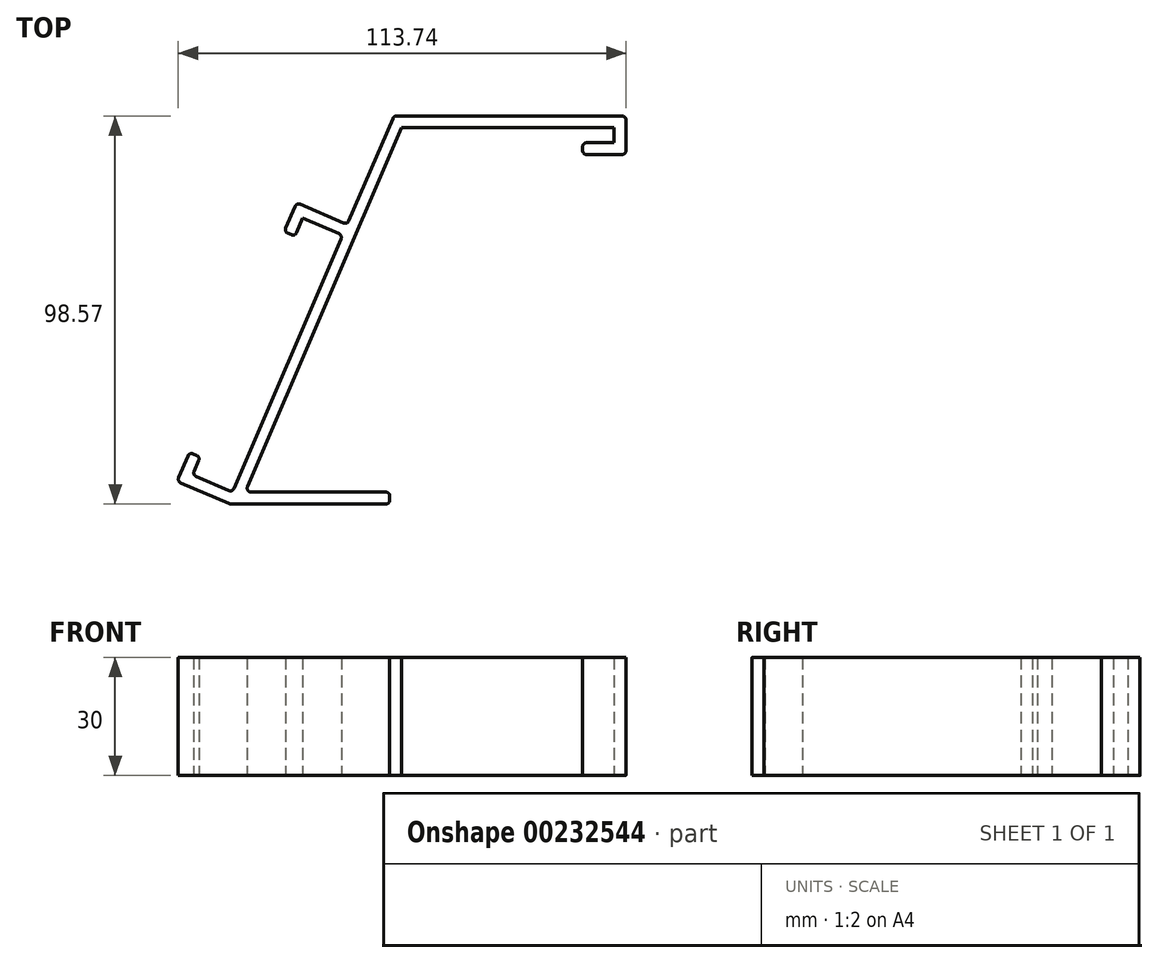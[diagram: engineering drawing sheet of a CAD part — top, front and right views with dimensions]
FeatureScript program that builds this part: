
annotation { "Feature Type Name" : "Feature", "Feature Type Description" : "" }
export const myFeature = defineFeature(function(context is Context, id is Id, definition is map)
    precondition{}
    {
        {
            var Q0;
            Q0=qCreatedBy(makeId("Top.planeOp"),FACE);
            var sketch = newSketch(context, id + "F0", { "sketchPlane" : qUnion([Q0])});
            skLineSegment(sketch, "E0", {"start": v(12.49, -12.5) * mm, "end": v(19.49, -12.5) * mm});
            skLineSegment(sketch, "E1", {"start": v(19.49, -12.5) * mm, "end": v(19.49, -8.7) * mm});
            skLineSegment(sketch, "E2", {"start": v(19.49, -8.7) * mm, "end": v(-34.51, -8.7) * mm});
            skLineSegment(sketch, "E3", {"start": v(21.5, -15.5) * mm, "end": v(12.49, -15.5) * mm});
            skLineSegment(sketch, "E4", {"start": v(11.49, -13.49) * mm, "end": v(11.49, -14.5) * mm});
            skLineSegment(sketch, "E5", {"start": v(-34.51, -8.7) * mm, "end": v(-73.65, -99.87) * mm});
            skLineSegment(sketch, "E6", {"start": v(-72.73, -101.26) * mm, "end": v(-38.5, -101.26) * mm});
            skLineSegment(sketch, "E7", {"start": v(-37.51, -102.26) * mm, "end": v(-37.51, -103.26) * mm});
            skLineSegment(sketch, "E8", {"start": v(-38.5, -104.26) * mm, "end": v(-77.92, -104.26) * mm});
            skLineSegment(sketch, "E9", {"start": v(-86.7, -97.31) * mm, "end": v(-78.43, -100.86) * mm});
            skLineSegment(sketch, "E10", {"start": v(-77.12, -100.34) * mm, "end": v(-49.9, -36.93) * mm});
            skLineSegment(sketch, "E11", {"start": v(-87.23, -96) * mm, "end": v(-86.04, -93.24) * mm});
            skLineSegment(sketch, "E12", {"start": v(-86.56, -91.93) * mm, "end": v(-87.49, -91.53) * mm});
            skLineSegment(sketch, "E13", {"start": v(-88.8, -92.06) * mm, "end": v(-91.17, -97.58) * mm});
            skLineSegment(sketch, "E14", {"start": v(-90.64, -98.89) * mm, "end": v(-78.32, -104.18) * mm});
            skLineSegment(sketch, "E15", {"start": v(-50.42, -35.62) * mm, "end": v(-59.61, -31.68) * mm});
            skLineSegment(sketch, "E16", {"start": v(-59.61, -31.68) * mm, "end": v(-61.2, -35.35) * mm});
            skLineSegment(sketch, "E17", {"start": v(-62.5, -35.88) * mm, "end": v(-63.43, -35.48) * mm});
            skLineSegment(sketch, "E18", {"start": v(-63.95, -34.17) * mm, "end": v(-61.58, -28.65) * mm});
            skLineSegment(sketch, "E19", {"start": v(-60.27, -28.13) * mm, "end": v(-49.24, -32.86) * mm});
            skLineSegment(sketch, "E20.trimOffspring", {"start": v(-47.93, -32.34) * mm, "end": v(-36.75, -6.3) * mm});
            skLineSegment(sketch, "E21", {"start": v(22.49, -14.5) * mm, "end": v(22.49, -6.69) * mm});
            skLineSegment(sketch, "E22", {"start": v(-35.83, -5.7) * mm, "end": v(21.5, -5.7) * mm});
            skPoint(sketch, "E23.visualSharp", {"position": v(11.49, -12.5) * mm});
            skArc(sketch, "E23.filletArc", {"start": v(12.49, -12.5) * mm, "mid": v(11.78, -12.78) * mm, "end": v(11.49, -13.49) * mm});
            skPoint(sketch, "E24.visualSharp", {"position": v(11.49, -15.5) * mm});
            skArc(sketch, "E24.filletArc", {"start": v(11.49, -14.5) * mm, "mid": v(11.78, -15.2) * mm, "end": v(12.49, -15.5) * mm});
            skPoint(sketch, "E25.visualSharp", {"position": v(22.49, -15.5) * mm});
            skArc(sketch, "E25.filletArc", {"start": v(21.5, -15.5) * mm, "mid": v(22.2, -15.2) * mm, "end": v(22.49, -14.5) * mm});
            skPoint(sketch, "E26.visualSharp", {"position": v(22.49, -5.7) * mm});
            skArc(sketch, "E26.filletArc", {"start": v(22.49, -6.69) * mm, "mid": v(22.2, -5.98) * mm, "end": v(21.5, -5.7) * mm});
            skPoint(sketch, "E27.visualSharp", {"position": v(-36.49, -5.7) * mm});
            skArc(sketch, "E27.filletArc", {"start": v(-35.83, -5.7) * mm, "mid": v(-36.38, -5.86) * mm, "end": v(-36.75, -6.3) * mm});
            skPoint(sketch, "E28.visualSharp", {"position": v(-61.19, -27.74) * mm});
            skArc(sketch, "E28.filletArc", {"start": v(-60.27, -28.13) * mm, "mid": v(-61.03, -28.12) * mm, "end": v(-61.58, -28.65) * mm});
            skPoint(sketch, "E29.visualSharp", {"position": v(-64.34, -35.09) * mm});
            skArc(sketch, "E29.filletArc", {"start": v(-63.95, -34.17) * mm, "mid": v(-63.96, -34.93) * mm, "end": v(-63.43, -35.48) * mm});
            skPoint(sketch, "E30.visualSharp", {"position": v(-61.58, -36.27) * mm});
            skArc(sketch, "E30.filletArc", {"start": v(-62.5, -35.88) * mm, "mid": v(-61.74, -35.89) * mm, "end": v(-61.2, -35.35) * mm});
            skPoint(sketch, "E31.visualSharp", {"position": v(-48.32, -33.26) * mm});
            skArc(sketch, "E31.filletArc", {"start": v(-49.24, -32.86) * mm, "mid": v(-48.47, -32.87) * mm, "end": v(-47.93, -32.34) * mm});
            skPoint(sketch, "E32.visualSharp", {"position": v(-49.5, -36.01) * mm});
            skArc(sketch, "E32.filletArc", {"start": v(-49.9, -36.93) * mm, "mid": v(-49.89, -36.17) * mm, "end": v(-50.42, -35.62) * mm});
            skPoint(sketch, "E33.visualSharp", {"position": v(-77.51, -101.26) * mm});
            skArc(sketch, "E33.filletArc", {"start": v(-78.43, -100.86) * mm, "mid": v(-77.66, -100.87) * mm, "end": v(-77.12, -100.34) * mm});
            skPoint(sketch, "E34.visualSharp", {"position": v(-78.13, -104.26) * mm});
            skArc(sketch, "E34.filletArc", {"start": v(-78.32, -104.18) * mm, "mid": v(-78.12, -104.24) * mm, "end": v(-77.92, -104.26) * mm});
            skPoint(sketch, "E35.visualSharp", {"position": v(-74.25, -101.26) * mm});
            skArc(sketch, "E35.filletArc", {"start": v(-73.65, -99.87) * mm, "mid": v(-73.57, -100.8) * mm, "end": v(-72.73, -101.26) * mm});
            skPoint(sketch, "E36.visualSharp", {"position": v(-87.62, -96.92) * mm});
            skArc(sketch, "E36.filletArc", {"start": v(-87.23, -96) * mm, "mid": v(-87.24, -96.77) * mm, "end": v(-86.7, -97.31) * mm});
            skPoint(sketch, "E37.visualSharp", {"position": v(-85.65, -92.32) * mm});
            skArc(sketch, "E37.filletArc", {"start": v(-86.04, -93.24) * mm, "mid": v(-86.03, -92.48) * mm, "end": v(-86.56, -91.93) * mm});
            skPoint(sketch, "E38.visualSharp", {"position": v(-88.4, -91.14) * mm});
            skArc(sketch, "E38.filletArc", {"start": v(-87.49, -91.53) * mm, "mid": v(-88.25, -91.52) * mm, "end": v(-88.8, -92.06) * mm});
            skPoint(sketch, "E39.visualSharp", {"position": v(-91.56, -98.5) * mm});
            skArc(sketch, "E39.filletArc", {"start": v(-91.17, -97.58) * mm, "mid": v(-91.18, -98.34) * mm, "end": v(-90.64, -98.89) * mm});
            skPoint(sketch, "E40.visualSharp", {"position": v(-37.51, -104.26) * mm});
            skArc(sketch, "E40.filletArc", {"start": v(-38.5, -104.26) * mm, "mid": v(-37.8, -103.97) * mm, "end": v(-37.51, -103.26) * mm});
            skPoint(sketch, "E41.visualSharp", {"position": v(-37.51, -101.26) * mm});
            skArc(sketch, "E41.filletArc", {"start": v(-37.51, -102.26) * mm, "mid": v(-37.8, -101.55) * mm, "end": v(-38.5, -101.26) * mm});
            skSolve(sketch);
        }
        {
            var Q0;
            Q0=makeQuery(id+"F0.imprint","IMPRINT",FACE,{"disambiguationData":[TD([[makeQuery(id+"F0.imprint","IMPRINT",EDGE,{"derivedFrom":sQuery(id+"F0.wireOp",EDGE,"E0")}),-1.0]])]});
            extrude(context, id + "F1", {"entities" : qUnion([Q0]), "depth" : 30 * mm});
        }
    });
